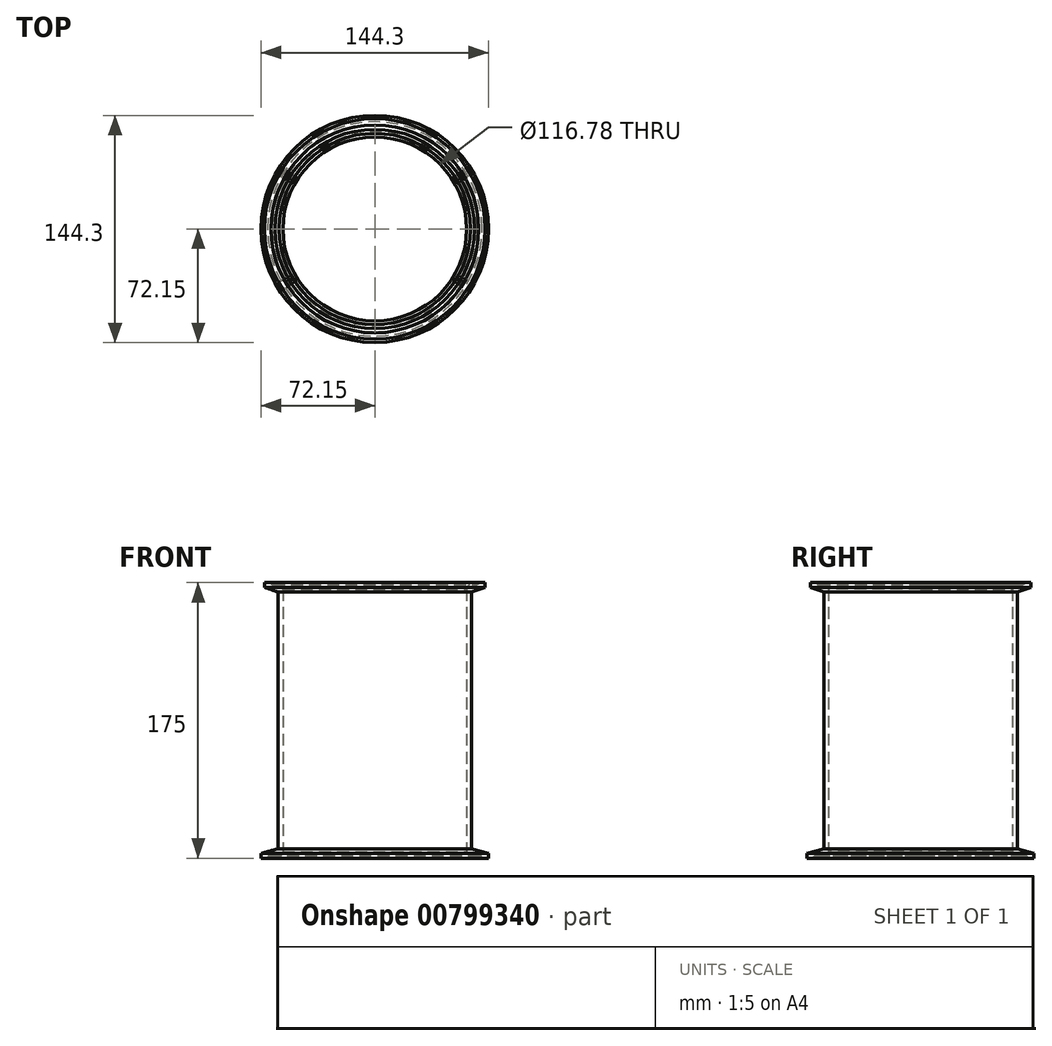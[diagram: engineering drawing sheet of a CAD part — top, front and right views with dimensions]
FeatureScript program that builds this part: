
annotation { "Feature Type Name" : "Feature", "Feature Type Description" : "" }
export const myFeature = defineFeature(function(context is Context, id is Id, definition is map)
    precondition{}
    {
        {
            var Q0;
            Q0=qCreatedBy(makeId("Front.planeOp"),FACE);
            var sketch = newSketch(context, id + "F0", { "sketchPlane" : qUnion([Q0])});
            skLineSegment(sketch, "E0", {"start": v(-61.39, 0) * mm, "end": v(-65.37, 0) * mm});
            skLineSegment(sketch, "E1", {"start": v(-58.4, 175) * mm, "end": v(-58.4, 0) * mm});
            skLineSegment(sketch, "E2", {"start": v(-61.39, 0) * mm, "end": v(-58.4, 0) * mm});
            skLineSegment(sketch, "E3", {"start": v(-72.15, 0) * mm, "end": v(-72.15, 3) * mm});
            skPoint(sketch, "E3.endSnap0", {"position": v(-61.39, 3) * mm});
            skLineSegment(sketch, "E4", {"start": v(-61.39, 6) * mm, "end": v(-72.15, 3) * mm});
            skArc(sketch, "E5", {"start": v(-65.37, 0) * mm, "mid": v(-66.74, 1.37) * mm, "end": v(-68.1, 0) * mm});
            skLineSegment(sketch, "E6.trimOffspring", {"start": v(-68.1, 0) * mm, "end": v(-72.15, 0) * mm});
            skLineSegment(sketch, "E7", {"start": v(0, 0) * mm, "end": v(0, 38.79) * mm, "construction": true});
            skLineSegment(sketch, "E8.MirrorCS", {"start": v(-63.26, 175) * mm, "end": v(-63.5, 175) * mm});
            skLineSegment(sketch, "E9.MirrorCS", {"start": v(-66, 175) * mm, "end": v(-70.04, 175) * mm});
            skArc(sketch, "E10.MirrorCS", {"start": v(-63.26, 175) * mm, "mid": v(-64.63, 173.63) * mm, "end": v(-66, 175) * mm});
            skLineSegment(sketch, "E11.MirrorCS", {"start": v(-70.04, 175) * mm, "end": v(-70.04, 172) * mm});
            skLineSegment(sketch, "E12.MirrorCS", {"start": v(-63.5, 175) * mm, "end": v(-58.4, 175) * mm});
            skLineSegment(sketch, "E13.MirrorCS", {"start": v(-61.4, 169) * mm, "end": v(-70.04, 172) * mm});
            skPoint(sketch, "E14.MirrorP", {"position": v(-63.5, 172) * mm});
            skLineSegment(sketch, "E15", {"start": v(-61.39, 6) * mm, "end": v(-61.4, 169) * mm});
            skSolve(sketch);
        }
        {
            var Q0;
            Q0=qSketchRegion(id+"F0",true);
            var Q1;
            Q1=sQuery(id+"F0.wireOp",EDGE,"E7");
            revolve(context, id + "F1", {"entities" : qUnion([Q0]), "axis" : qUnion([Q1]), "revolveType" : RevolveType.FULL});
        }
        {
            var Q0;
            Q0=makeQuery(id+"F1.opRevolve","SWEPT_EDGE",EDGE,{"disambiguationData":[OSD([sQuery(id+"F0.wireOp",EDGE,"E1"),sQuery(id+"F0.wireOp",EDGE,"E2")])]});
            var Q1;
            Q1=makeQuery(id+"F1.opRevolve","SWEPT_EDGE",EDGE,{"disambiguationData":[OSD([sQuery(id+"F0.wireOp",EDGE,"E1"),sQuery(id+"F0.wireOp",EDGE,"E12.MirrorCS")])]});
            chamfer(context, id + "F2", {"entities" : qUnion([Q0, Q1]), "chamferType" : ChamferType.OFFSET_ANGLE, "width" : 4 * mm, "oppositeDirection" : false, "angle" : 30 * degree, "tangentPropagation" : true});
        }
    });
